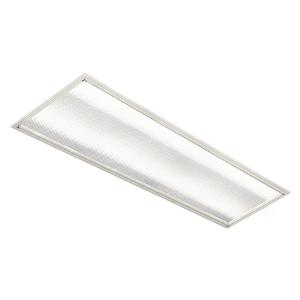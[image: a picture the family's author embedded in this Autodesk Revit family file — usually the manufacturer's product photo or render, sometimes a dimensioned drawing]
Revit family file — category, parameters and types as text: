
# Revit family: 3f_filippi_-_l_320_sp_3f_filippi_-_21293_-_l_322x18w_led_ep_sp_296x1196
name_source: partatom
category: Lighting Fixtures
units: mm (PartAtom-declared; Revit-internal decimal feet)

## family parameters
Cut with Voids When Loaded = No
Host = Face
Light Source = No
Part Type = Normal
Room Calculation Point = No
Round Connector Dimension = Use Diameter
Shared = No

## types (1)
- 3F Filippi - L 320 SP (1 x LED, 5114 lm, 41 W, 4000 K)
    Apparent Load = 41 VA
    Approval mark = ENEC
    CIE Flux Codes = 61 91 99 100 100
    Color Rendering = 80
    Color Temperature = 4000 K
    Control Gear = Electronic ballast
    Default Elevation = 1800 mm
    Description = ILLUMINOTECHNICAL
Luminous efficiency 100% (DLOR 100%, ULOR 0%).
Initial luminous flux of the luminaire 5114 lm.
Emergency luminaire luminous flux BLF 9.5%.
Direct symmetric distribution.
Installation Interdistance Transv.D = 1.17 x hu - Long.D = 1.20 x hu.
Average luminance <3000 cd/m² for radial angles >65°.
Tabular UGR (CIE 117 - 4H-8H; S=0.25H; 70/50/20): RUG 18.4 - 19.1.
Beam angle: 91° - 95°.
Luminous efficacy 125 lm/W.
Lifetime (L93/B10): 30000 h. (tq+25°C)
Lifetime (L90/B10): 50000 h. (tq+25°C)
Lifetime (L85/B10): 80000 h. (tq+25°C)
Lifetime (L80/B10): 100000 h. (tq+25°C)
Sudden decreased luminous flux after 50000 hours: 0% (C0).
Photobiological safety in compliance with IEC/TR 62778: RG0 risk exempt, (IEC 62471).
In compliance with IEC/EN 62722-2-1 - IEC/EN 62717 standards.

SOURCE
2 linear LED modules 18W/840.
Energy efficiency class (UE 2019/2020 - UE 2019/2015): D.
CIE 13.3 Colour rendering index: CRI >80 (R9 <50%).
IES TM-30 Fidelity Index: Rf = 84 Rg = 95.
CCT nominal colour temperature 4000 K.
Colour initial tolerance (MacAdam): SDCM 2.

MECHANICAL
Steel body, painted in white polyester.
Transparent methacrylate (PMMA) flat diffuser, multilenticular exterior, anti-glare, locked to the white painted aluminium perimeter frame with sealing gasket, hinged opening.
Luminaire with limited surface temperature. - D - (EN 60598-2-24)
Dimensions: 1196x296 mm, height 95 mm. Weight 5.385 kg.
IP54 protection degree for exposed part, IP20 for recessed part.
Mechanical strength to impacts IK06 (1 joule).
Glow-wire test resistance 650°C.

ELECTRICAL
Halogen Free electronic wiring 230V-50/60Hz, power factor 0.90, THD <25%, constant output current, SELV, class I, 1 driver.
Power of the luminaire 41 W.
CE - IEC 60598-1 - EN 60598-1.
EP maintained emergency wiring on board, 1h duration, 24h recharge; compliant with EN 60598-2-22, excluding high risk areas.
SAFE FLICKER: PstLM=<1 and SVM=<0.4 (IEC TR 61547-1 and IEC TR 63158), to ensure a more comfortable and safe light.
Ambient temperature from +5°C to +25°C.
Temperature class T6 max 85°C.
Relative humidity UR: <85%.

INSTALLATION
Lay-in recessed fitting / Pull-up recessed fitting with brackets.
False ceiling carving: 280x1180 mm.
All accessories dedicated to this product are available on the Catalog and on our website www.3F-Filippi.com.

APPLICATIONS
Suitable product for food production plants (HACCP), IFS (Food Version 6), BRC (GSFS Food Version 7).
Environments: sterilized, aseptic.
In environments with VDU's, managerial offices and staterooms, environments involving accurate visual tasks where a diffused and soft light for an optimum visual comfort and the source total shielding are required.

WARNING
Luminaire designed for disposal/recycling at end-of-life.
Replaceable (LED only) light source by a professional. Replaceable control gear by a professional.
    Height = 0 mm  [stored 0 ft]
    Lamp = 1 x LED
    Lamp Light Flux = 5114 lm
    Lamp Power = 41 W
    Lamp count = 1
    Length = 1196 mm
    Lifetime = 50000 h
    Luminous efficacy = 125 lm/W
    Manufacturer = 3F Filippi
    ModVariant = No
    Model = 3F Filippi - 21293 - L 322x18W LED EP SP 296x1196
    Mounting Place = Ceiling
    Mounting Type = Recessed
    Number of Poles = 1
    OnlyDefault = Yes
    Power Factor = 1
    Product Name = 3F Filippi - L 320 SP
    Product group = recessed luminaire
    ProductGroupID = 4
    Protection Class = Protection class I
    Protection Degree = IP 20
    RLX_Detail_Level = 1
    RLX_Emergency_Light_Flux = 0 lm
    RLX_Emergency_Type = 0
    RLX_Emergency_Type_DB = No
    RlxData = <blob elided: 35745 chars, md5=a3d482ca>
    Socket = socket
    Standby Power = 0 W
    System Light Flux = 5114 lm
    System Power = 41 W
    Type Comments = Product without accessories
    Type Image = 3ffilippi_l_320_led_sp_1196.jpg
    URL = http://relux.com
    VarID = ---
    Voltage = 0 V
    Weight = 0.00 kg
    Width = 296 mm

note: [stored X ft] marks values corroborated as IEEE doubles in the binary element streams (Revit-internal decimal feet)

## geometry (parser evidence)
native form markers: Blend x4, Sweep x10
no freeform markers — native parametric forms only
